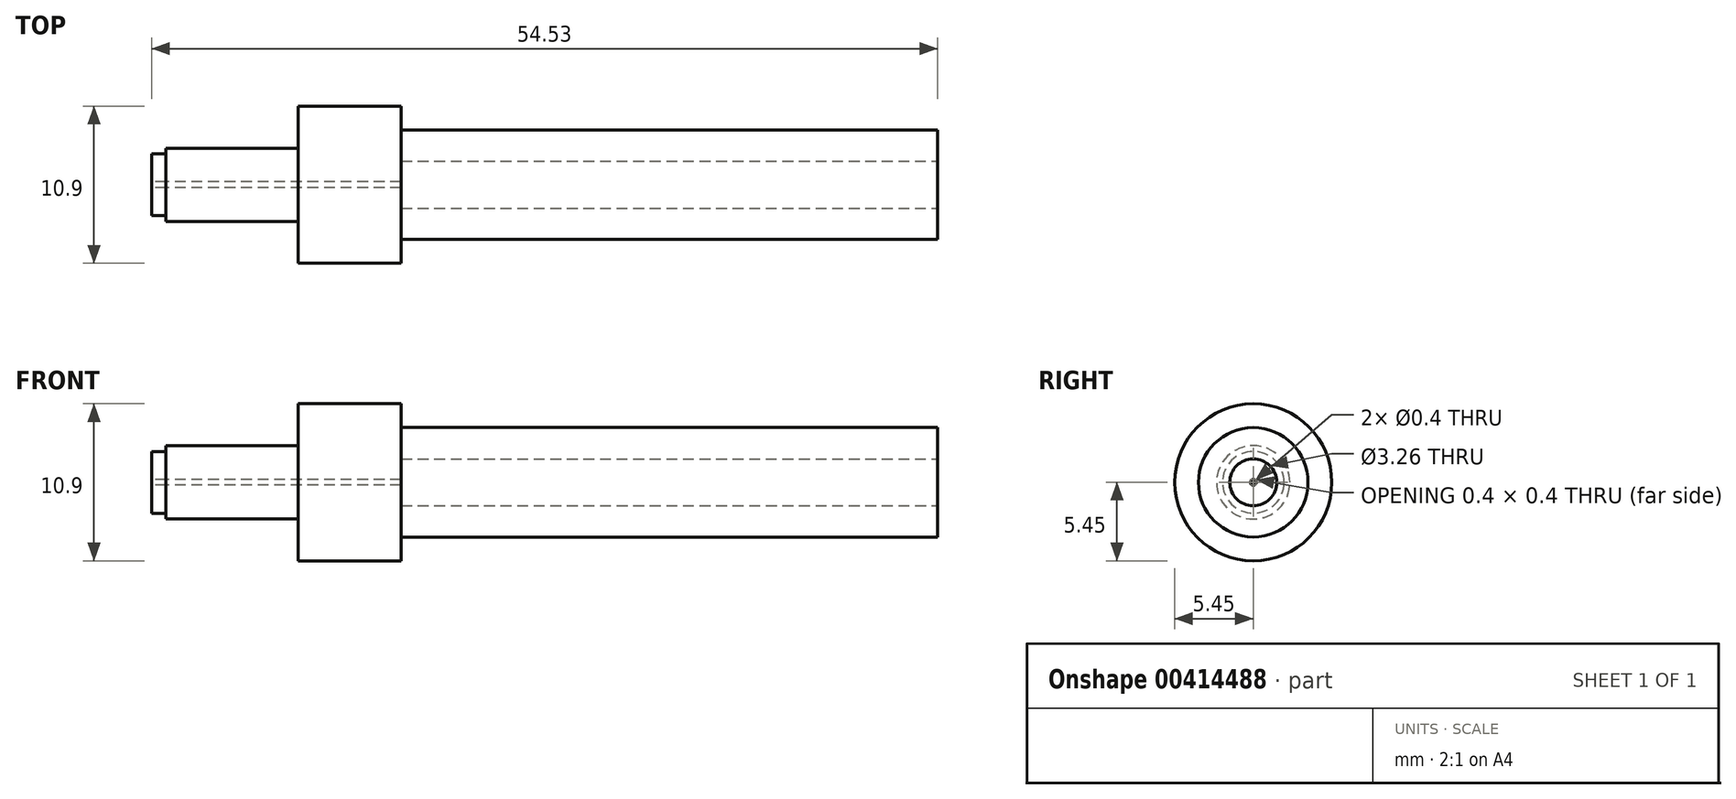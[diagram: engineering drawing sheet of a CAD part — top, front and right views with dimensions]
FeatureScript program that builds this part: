
annotation { "Feature Type Name" : "Feature", "Feature Type Description" : "" }
export const myFeature = defineFeature(function(context is Context, id is Id, definition is map)
    precondition{}
    {
        {
            var Q0;
            Q0=qCreatedBy(makeId("Front.planeOp"),FACE);
            var sketch = newSketch(context, id + "F0", { "sketchPlane" : qUnion([Q0])});
            skLineSegment(sketch, "E0.bottom", {"start": v(0, 3.8) * mm, "end": v(37.22, 3.8) * mm});
            skLineSegment(sketch, "E0.top", {"start": v(0, 1.63) * mm, "end": v(37.22, 1.63) * mm});
            skLineSegment(sketch, "E0.left", {"start": v(0, 3.8) * mm, "end": v(0, 1.63) * mm});
            skLineSegment(sketch, "E0.right", {"start": v(37.22, 3.8) * mm, "end": v(37.22, 1.63) * mm});
            skLineSegment(sketch, "E1", {"start": v(59.54, 0) * mm, "end": v(-39.8, 0) * mm, "construction": true});
            skSolve(sketch);
        }
        {
            var Q0;
            Q0=qCreatedBy(makeId("Front.planeOp"),FACE);
            var sketch = newSketch(context, id + "F1", { "sketchPlane" : qUnion([Q0])});
            skLineSegment(sketch, "E2", {"start": v(0, 0) * mm, "end": v(0, 5.45) * mm});
            skLineSegment(sketch, "E3", {"start": v(0, 5.45) * mm, "end": v(-7.13, 5.45) * mm});
            skLineSegment(sketch, "E4", {"start": v(-7.13, 5.45) * mm, "end": v(-7.13, 2.55) * mm});
            skLineSegment(sketch, "E5", {"start": v(-7.13, 2.55) * mm, "end": v(-16.31, 2.55) * mm});
            skLineSegment(sketch, "E6", {"start": v(-16.31, 2.55) * mm, "end": v(-16.31, 0) * mm});
            skLineSegment(sketch, "E7", {"start": v(-16.3, 0) * mm, "end": v(0, 0) * mm});
            skSolve(sketch);
        }
        {
            var Q0;
            Q0=qCreatedBy(makeId("Front.planeOp"),FACE);
            var sketch = newSketch(context, id + "F2", { "sketchPlane" : qUnion([Q0])});
            skLineSegment(sketch, "E8.bottom", {"start": v(-16.31, 0) * mm, "end": v(-17.31, 0) * mm});
            skLineSegment(sketch, "E8.top", {"start": v(-16.31, 2.14) * mm, "end": v(-17.31, 2.14) * mm});
            skLineSegment(sketch, "E8.left", {"start": v(-16.31, 0) * mm, "end": v(-16.31, 2.14) * mm});
            skLineSegment(sketch, "E8.right", {"start": v(-17.31, 0) * mm, "end": v(-17.31, 2.14) * mm});
            skSolve(sketch);
        }
        {
            var Q0;
            Q0=makeQuery(id+"F0.imprint","IMPRINT",FACE,{"disambiguationData":[TD([[makeQuery(id+"F0.imprint","IMPRINT",EDGE,{"derivedFrom":sQuery(id+"F0.wireOp",EDGE,"E0.bottom")}),-1.0]])]});
            var Q1;
            Q1=sQuery(id+"F0.wireOp",EDGE,"E1");
            revolve(context, id + "F3", {"entities" : qUnion([Q0]), "axis" : qUnion([Q1]), "revolveType" : RevolveType.FULL});
        }
        {
            var Q0;
            Q0 = qSketchRegion(id + "F1", true);
            var Q1;
            Q1=sQuery(id+"F1.wireOp",EDGE,"E7");
            revolve(context, id + "F4", {"entities" : qUnion([Q0]), "axis" : qUnion([Q1]), "revolveType" : RevolveType.FULL});
        }
        {
            var Q0;
            Q0 = qSketchRegion(id + "F2", true);
            var Q1;
            Q1=sQuery(id+"F2.wireOp",EDGE,"E8.bottom");
            revolve(context, id + "F5", {"entities" : qUnion([Q0]), "axis" : qUnion([Q1]), "revolveType" : RevolveType.FULL});
        }
        {
            var Q0;
            Q0=makeQuery(id+"F5.opRevolve","SWEPT_FACE",FACE,{"disambiguationData":[OSD([sQuery(id+"F2.wireOp",EDGE,"E8.right")])]});
            var sketch = newSketch(context, id + "F6", { "sketchPlane" : qUnion([Q0])});
            skCircle(sketch, "E9", {"center": v(0, 0) * mm, "radius": 0.2 * mm});
            skSolve(sketch);
        }
        {
            var Q0;
            Q0 = qSketchRegion(id + "F6", true);
            extrude(context, id + "F7", {"entities" : qUnion([Q0]), "operationType" : NewBodyOperationType.REMOVE, "endBound" : BoundingType.THROUGH_ALL, "oppositeDirection" : true, "depth" : 25 * mm});
        }
    });
